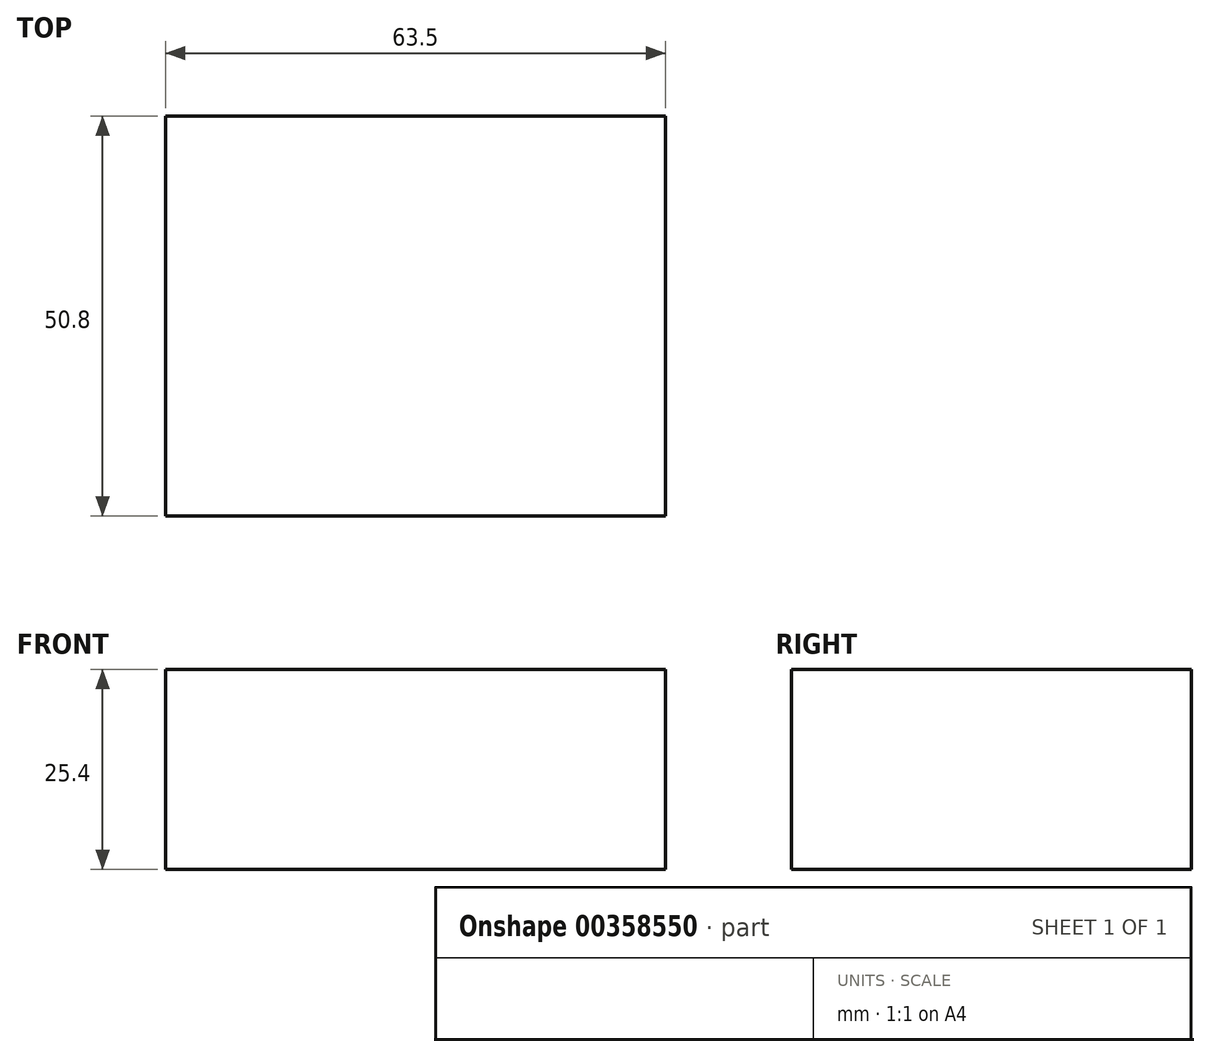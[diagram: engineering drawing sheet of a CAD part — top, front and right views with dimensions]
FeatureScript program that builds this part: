
annotation { "Feature Type Name" : "Feature", "Feature Type Description" : "" }
export const myFeature = defineFeature(function(context is Context, id is Id, definition is map)
    precondition{}
    {
        {
            var Q0;
            Q0=qCreatedBy(makeId("Top.planeOp"),FACE);
            var sketch = newSketch(context, id + "F0", { "sketchPlane" : qUnion([Q0])});
            skLineSegment(sketch, "E0.bottom", {"start": v(0, 0) * mm, "end": v(63.5, 0) * mm});
            skLineSegment(sketch, "E0.top", {"start": v(0, -50.8) * mm, "end": v(63.5, -50.8) * mm});
            skLineSegment(sketch, "E0.left", {"start": v(0, 0) * mm, "end": v(0, -50.8) * mm});
            skLineSegment(sketch, "E0.right", {"start": v(63.5, 0) * mm, "end": v(63.5, -50.8) * mm});
            skSolve(sketch);
        }
        {
            var Q0;
            Q0=makeQuery(id+"F0.imprint","IMPRINT",FACE,{"disambiguationData":[TD([[makeQuery(id+"F0.imprint","IMPRINT",EDGE,{"derivedFrom":sQuery(id+"F0.wireOp",EDGE,"E0.bottom")}),-1.0]])]});
            extrude(context, id + "F1", {"entities" : qUnion([Q0]), "depth" : 25.4 * mm});
        }
    });
